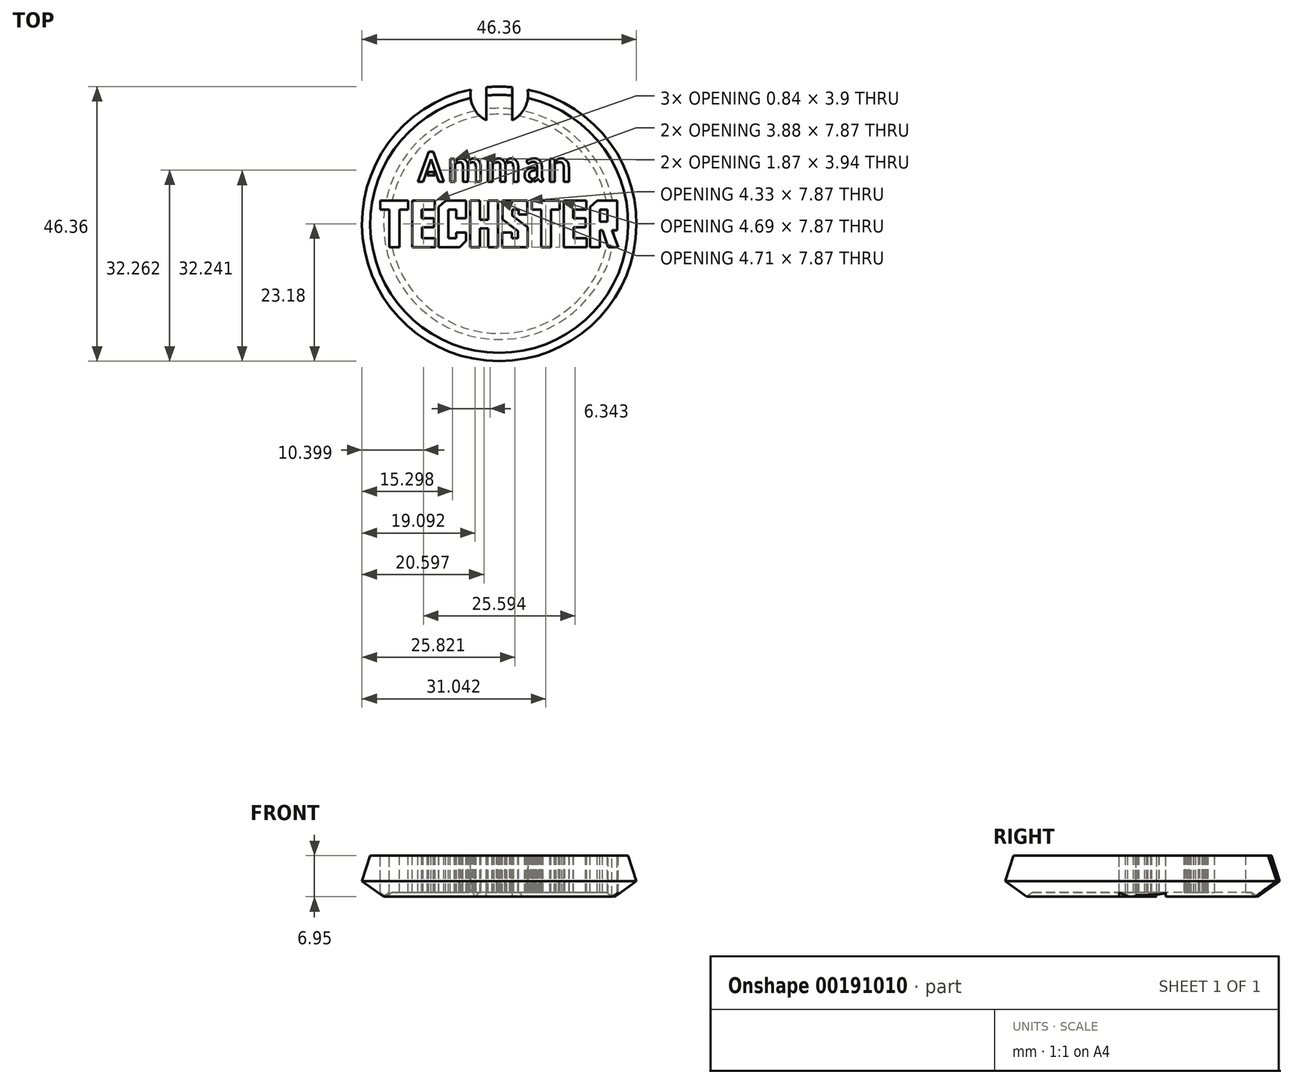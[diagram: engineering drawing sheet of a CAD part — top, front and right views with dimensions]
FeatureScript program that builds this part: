
annotation { "Feature Type Name" : "Feature", "Feature Type Description" : "" }
export const myFeature = defineFeature(function(context is Context, id is Id, definition is map)
    precondition{}
    {
        {
            var Q0;
            Q0=qCreatedBy(makeId("Front.planeOp"),FACE);
            var sketch = newSketch(context, id + "F0", { "sketchPlane" : qUnion([Q0])});
            skLineSegment(sketch, "E0.bottom", {"start": v(0, 0) * mm, "end": v(-19.52, 0) * mm});
            skLineSegment(sketch, "E0.top", {"start": v(0, 6.22) * mm, "end": v(-19.52, 6.22) * mm});
            skLineSegment(sketch, "E0.left", {"start": v(0, 0) * mm, "end": v(0, 6.22) * mm});
            skLineSegment(sketch, "E0.right", {"start": v(-19.52, 0) * mm, "end": v(-19.52, 6.22) * mm});
            skCircle(sketch, "E1.cCircle", {"center": v(-19.52, 3.1) * mm, "radius": 3.1 * mm, "construction": true});
            skLineSegment(sketch, "E1.0", {"start": v(-21.78, 6.22) * mm, "end": v(-17.27, 6.22) * mm});
            skLineSegment(sketch, "E1.1", {"start": v(-17.27, 6.22) * mm, "end": v(-15.87, 1.92) * mm});
            skLineSegment(sketch, "E1.2", {"start": v(-15.87, 1.92) * mm, "end": v(-19.52, -0.73) * mm});
            skLineSegment(sketch, "E1.3", {"start": v(-19.52, -0.73) * mm, "end": v(-23.18, 1.92) * mm});
            skLineSegment(sketch, "E1.4", {"start": v(-23.18, 1.92) * mm, "end": v(-21.78, 6.22) * mm});
            skPoint(sketch, "E1.0.midPoint", {"position": v(-19.52, 6.22) * mm});
            skSolve(sketch);
        }
        {
            var Q0;
            Q0 = qSketchRegion(id + "F0", true);
            var Q1;
            Q1=sQuery(id+"F0.wireOp",EDGE,"E0.left");
            revolve(context, id + "F1", {"entities" : qUnion([Q0]), "axis" : qUnion([Q1]), "revolveType" : RevolveType.FULL});
        }
        {
            var Q0;
            Q0=qCreatedBy(makeId("Top.planeOp"),FACE);
            cPlane(context, id + "F2", {"entities" : qUnion([Q0]), "cplaneType" : CPlaneType.OFFSET, "offset" : 8 * mm, "width" : 152.4 * mm, "height" : 152.4 * mm});
        }
        {
            var Q0;
            Q0=qCreatedBy(id+"F2.planeOp",FACE);
            var sketch = newSketch(context, id + "F3", { "sketchPlane" : qUnion([Q0])});
            skLineSegment(sketch, "E2", {"start": v(-15.39, 2.44) * mm, "end": v(-16.87, 2.44) * mm});
            skLineSegment(sketch, "E3", {"start": v(-16.87, 2.44) * mm, "end": v(-16.87, -3.94) * mm});
            skLineSegment(sketch, "E4", {"start": v(-16.87, -3.94) * mm, "end": v(-18.54, -3.94) * mm});
            skLineSegment(sketch, "E5", {"start": v(-18.54, -3.94) * mm, "end": v(-18.54, 2.44) * mm});
            skLineSegment(sketch, "E6", {"start": v(-18.54, 2.44) * mm, "end": v(-20.08, 2.44) * mm});
            skLineSegment(sketch, "E7", {"start": v(-20.08, 2.44) * mm, "end": v(-20.08, 3.94) * mm});
            skLineSegment(sketch, "E8", {"start": v(-20.08, 3.94) * mm, "end": v(-15.39, 3.94) * mm});
            skLineSegment(sketch, "E9", {"start": v(-15.39, 3.94) * mm, "end": v(-15.39, 2.44) * mm});
            skLineSegment(sketch, "E10", {"start": v(-14.72, 3.94) * mm, "end": v(-10.9, 3.94) * mm});
            skLineSegment(sketch, "E11", {"start": v(-10.9, 3.94) * mm, "end": v(-10.9, 2.44) * mm});
            skLineSegment(sketch, "E12", {"start": v(-10.9, 2.44) * mm, "end": v(-13.09, 2.44) * mm});
            skLineSegment(sketch, "E13", {"start": v(-13.09, 2.44) * mm, "end": v(-13.09, 0.92) * mm});
            skLineSegment(sketch, "E14", {"start": v(-13.09, 0.92) * mm, "end": v(-11, 0.92) * mm});
            skLineSegment(sketch, "E15", {"start": v(-11, 0.92) * mm, "end": v(-11, -0.55) * mm});
            skLineSegment(sketch, "E16", {"start": v(-11, -0.55) * mm, "end": v(-13.06, -0.55) * mm});
            skLineSegment(sketch, "E17", {"start": v(-13.06, -0.55) * mm, "end": v(-13.06, -2.44) * mm});
            skLineSegment(sketch, "E18", {"start": v(-13.06, -2.44) * mm, "end": v(-10.84, -2.44) * mm});
            skLineSegment(sketch, "E19", {"start": v(-10.84, -2.44) * mm, "end": v(-10.84, -3.94) * mm});
            skLineSegment(sketch, "E20", {"start": v(-10.84, -3.94) * mm, "end": v(-14.72, -3.94) * mm});
            skLineSegment(sketch, "E21", {"start": v(-14.72, -3.94) * mm, "end": v(-14.72, 3.94) * mm});
            skLineSegment(sketch, "E22", {"start": v(-7.25, -2.44) * mm, "end": v(-7.25, -1.49) * mm});
            skLineSegment(sketch, "E23", {"start": v(-7.25, -1.49) * mm, "end": v(-5.6, -1.49) * mm});
            skLineSegment(sketch, "E24", {"start": v(-5.6, -1.49) * mm, "end": v(-5.6, -2.85) * mm});
            skLineSegment(sketch, "E25", {"start": v(-5.6, -2.85) * mm, "end": v(-6.69, -3.94) * mm});
            skLineSegment(sketch, "E26", {"start": v(-6.69, -3.94) * mm, "end": v(-10.24, -3.94) * mm});
            skLineSegment(sketch, "E27", {"start": v(-10.24, -3.94) * mm, "end": v(-10.24, 2.85) * mm});
            skLineSegment(sketch, "E28", {"start": v(-10.24, 2.85) * mm, "end": v(-9.06, 3.94) * mm});
            skLineSegment(sketch, "E29", {"start": v(-9.06, 3.94) * mm, "end": v(-5.6, 3.94) * mm});
            skLineSegment(sketch, "E30", {"start": v(-5.6, 3.94) * mm, "end": v(-5.6, 0.96) * mm});
            skLineSegment(sketch, "E31", {"start": v(-5.6, 0.96) * mm, "end": v(-7.25, 0.96) * mm});
            skLineSegment(sketch, "E32", {"start": v(-7.25, 0.96) * mm, "end": v(-7.25, 2.44) * mm});
            skLineSegment(sketch, "E33", {"start": v(-7.25, 2.44) * mm, "end": v(-8.58, 2.44) * mm});
            skLineSegment(sketch, "E34", {"start": v(-8.58, 2.44) * mm, "end": v(-8.58, -2.44) * mm});
            skLineSegment(sketch, "E35", {"start": v(-8.58, -2.44) * mm, "end": v(-7.25, -2.44) * mm});
            skLineSegment(sketch, "E36", {"start": v(-3.3, 0.7) * mm, "end": v(-1.88, 0.7) * mm});
            skLineSegment(sketch, "E37", {"start": v(-1.88, 0.7) * mm, "end": v(-1.88, 3.94) * mm});
            skLineSegment(sketch, "E38", {"start": v(-1.88, 3.94) * mm, "end": v(-0.23, 3.94) * mm});
            skLineSegment(sketch, "E39", {"start": v(-0.23, 3.94) * mm, "end": v(-0.23, -3.94) * mm});
            skLineSegment(sketch, "E40", {"start": v(-0.23, -3.94) * mm, "end": v(-1.88, -3.94) * mm});
            skLineSegment(sketch, "E41", {"start": v(-1.88, -3.94) * mm, "end": v(-1.88, -0.79) * mm});
            skLineSegment(sketch, "E42", {"start": v(-1.88, -0.79) * mm, "end": v(-3.3, -0.79) * mm});
            skLineSegment(sketch, "E43", {"start": v(-3.3, -0.79) * mm, "end": v(-3.3, -3.94) * mm});
            skLineSegment(sketch, "E44", {"start": v(-3.3, -3.94) * mm, "end": v(-4.94, -3.94) * mm});
            skLineSegment(sketch, "E45", {"start": v(-4.94, -3.94) * mm, "end": v(-4.94, 3.94) * mm});
            skLineSegment(sketch, "E46", {"start": v(-4.94, 3.94) * mm, "end": v(-3.3, 3.94) * mm});
            skLineSegment(sketch, "E47", {"start": v(-3.3, 3.94) * mm, "end": v(-3.3, 0.7) * mm});
            skLineSegment(sketch, "E48", {"start": v(4.8, -3.94) * mm, "end": v(0.48, -3.94) * mm});
            skLineSegment(sketch, "E49", {"start": v(0.48, -3.94) * mm, "end": v(0.48, -1.49) * mm});
            skLineSegment(sketch, "E50", {"start": v(0.48, -1.49) * mm, "end": v(2.13, -1.49) * mm});
            skLineSegment(sketch, "E51", {"start": v(2.13, -1.49) * mm, "end": v(2.13, -2.44) * mm});
            skLineSegment(sketch, "E52", {"start": v(2.13, -2.44) * mm, "end": v(3.15, -2.44) * mm});
            skLineSegment(sketch, "E53", {"start": v(3.15, -2.44) * mm, "end": v(3.15, -1.2) * mm});
            skLineSegment(sketch, "E54", {"start": v(3.15, -1.2) * mm, "end": v(0.53, 0.78) * mm});
            skLineSegment(sketch, "E55", {"start": v(0.53, 0.78) * mm, "end": v(0.53, 3.94) * mm});
            skLineSegment(sketch, "E56", {"start": v(0.53, 3.94) * mm, "end": v(4.76, 3.94) * mm});
            skLineSegment(sketch, "E57", {"start": v(4.76, 3.94) * mm, "end": v(4.76, 1.6) * mm});
            skLineSegment(sketch, "E58", {"start": v(4.76, 1.6) * mm, "end": v(3.26, 1.6) * mm});
            skLineSegment(sketch, "E59", {"start": v(3.26, 1.6) * mm, "end": v(3.26, 2.43) * mm});
            skLineSegment(sketch, "E60", {"start": v(3.26, 2.43) * mm, "end": v(2.18, 2.43) * mm});
            skLineSegment(sketch, "E61", {"start": v(2.18, 2.43) * mm, "end": v(2.18, 1.4) * mm});
            skLineSegment(sketch, "E62", {"start": v(2.18, 1.4) * mm, "end": v(4.8, -0.57) * mm});
            skLineSegment(sketch, "E63", {"start": v(4.8, -0.57) * mm, "end": v(4.8, -3.94) * mm});
            skLineSegment(sketch, "E64", {"start": v(10.2, 2.44) * mm, "end": v(8.72, 2.44) * mm});
            skLineSegment(sketch, "E65", {"start": v(8.72, 2.44) * mm, "end": v(8.72, -3.94) * mm});
            skLineSegment(sketch, "E66", {"start": v(8.72, -3.94) * mm, "end": v(7.06, -3.94) * mm});
            skLineSegment(sketch, "E67", {"start": v(7.06, -3.94) * mm, "end": v(7.06, 2.44) * mm});
            skLineSegment(sketch, "E68", {"start": v(7.06, 2.44) * mm, "end": v(5.52, 2.44) * mm});
            skLineSegment(sketch, "E69", {"start": v(5.52, 2.44) * mm, "end": v(5.52, 3.94) * mm});
            skLineSegment(sketch, "E70", {"start": v(5.52, 3.94) * mm, "end": v(10.2, 3.94) * mm});
            skLineSegment(sketch, "E71", {"start": v(10.2, 3.94) * mm, "end": v(10.2, 2.44) * mm});
            skLineSegment(sketch, "E72", {"start": v(10.88, 3.94) * mm, "end": v(14.7, 3.94) * mm});
            skLineSegment(sketch, "E73", {"start": v(14.7, 3.94) * mm, "end": v(14.7, 2.44) * mm});
            skLineSegment(sketch, "E74", {"start": v(14.7, 2.44) * mm, "end": v(12.5, 2.44) * mm});
            skLineSegment(sketch, "E75", {"start": v(12.5, 2.44) * mm, "end": v(12.5, 0.92) * mm});
            skLineSegment(sketch, "E76", {"start": v(12.5, 0.92) * mm, "end": v(14.59, 0.92) * mm});
            skLineSegment(sketch, "E77", {"start": v(14.59, 0.92) * mm, "end": v(14.59, -0.55) * mm});
            skLineSegment(sketch, "E78", {"start": v(14.59, -0.55) * mm, "end": v(12.53, -0.55) * mm});
            skLineSegment(sketch, "E79", {"start": v(12.53, -0.55) * mm, "end": v(12.53, -2.44) * mm});
            skLineSegment(sketch, "E80", {"start": v(12.53, -2.44) * mm, "end": v(14.75, -2.44) * mm});
            skLineSegment(sketch, "E81", {"start": v(14.75, -2.44) * mm, "end": v(14.75, -3.94) * mm});
            skLineSegment(sketch, "E82", {"start": v(14.75, -3.94) * mm, "end": v(10.88, -3.94) * mm});
            skLineSegment(sketch, "E83", {"start": v(10.88, -3.94) * mm, "end": v(10.88, 3.94) * mm});
            skLineSegment(sketch, "E84", {"start": v(18.42, -3.94) * mm, "end": v(17.44, -1.09) * mm});
            skLineSegment(sketch, "E85", {"start": v(17.44, -1.09) * mm, "end": v(17, -1.09) * mm});
            skLineSegment(sketch, "E86", {"start": v(17, -1.09) * mm, "end": v(17, -3.94) * mm});
            skLineSegment(sketch, "E87", {"start": v(17, -3.94) * mm, "end": v(15.36, -3.94) * mm});
            skLineSegment(sketch, "E88", {"start": v(15.36, -3.94) * mm, "end": v(15.36, 2.83) * mm});
            skLineSegment(sketch, "E89", {"start": v(15.36, 2.83) * mm, "end": v(16.55, 3.94) * mm});
            skLineSegment(sketch, "E90", {"start": v(16.55, 3.94) * mm, "end": v(19.92, 3.94) * mm});
            skLineSegment(sketch, "E91", {"start": v(19.92, 3.94) * mm, "end": v(19.92, -1.07) * mm});
            skLineSegment(sketch, "E92", {"start": v(19.92, -1.07) * mm, "end": v(19.03, -1.07) * mm});
            skLineSegment(sketch, "E93", {"start": v(19.03, -1.07) * mm, "end": v(20.08, -3.94) * mm});
            skLineSegment(sketch, "E94", {"start": v(20.08, -3.94) * mm, "end": v(18.42, -3.94) * mm});
            skLineSegment(sketch, "E95", {"start": v(18.27, 0.39) * mm, "end": v(18.27, 2.44) * mm});
            skLineSegment(sketch, "E96", {"start": v(18.27, 2.44) * mm, "end": v(17, 2.44) * mm});
            skLineSegment(sketch, "E97", {"start": v(17, 2.44) * mm, "end": v(17, 0.39) * mm});
            skLineSegment(sketch, "E98", {"start": v(17, 0.39) * mm, "end": v(18.27, 0.39) * mm});
            skSolve(sketch);
        }
        {
            var Q0;
            Q0 = qSketchRegion(id + "F3", true);
            extrude(context, id + "F4", {"entities" : qUnion([Q0]), "operationType" : NewBodyOperationType.REMOVE, "oppositeDirection" : true, "depth" : 25.4 * mm});
        }
        {
            var Q0;
            Q0=qCreatedBy(id+"F2.planeOp",FACE);
            var sketch = newSketch(context, id + "F5", { "sketchPlane" : qUnion([Q0])});
            skLineSegment(sketch, "E99.top", {"start": v(2.2, 26.67) * mm, "end": v(-2.2, 26.67) * mm});
            skLineSegment(sketch, "E99.left", {"start": v(2.2, 16.95) * mm, "end": v(2.2, 26.67) * mm});
            skLineSegment(sketch, "E99.right", {"start": v(-2.2, 16.95) * mm, "end": v(-2.2, 26.67) * mm});
            skPoint(sketch, "E99.middle", {"position": v(0, 21.81) * mm});
            skArc(sketch, "E100", {"start": v(2.2, 17.48) * mm, "mid": v(0, 26.67) * mm, "end": v(-2.2, 17.48) * mm});
            skSolve(sketch);
        }
        {
            var Q0;
            Q0 = qSketchRegion(id + "F5", true);
            extrude(context, id + "F6", {"entities" : qUnion([Q0]), "operationType" : NewBodyOperationType.REMOVE, "oppositeDirection" : true, "depth" : 25.4 * mm});
        }
        {
            var Q0;
            Q0=qCreatedBy(id+"F2.planeOp",FACE);
            var sketch = newSketch(context, id + "F7", { "sketchPlane" : qUnion([Q0])});
            skText(sketch, "E101", { "text": "Amman", "fontName": "AllertaStencil-Regular.ttf"});
            const initialGuessF7  = {"E101": [-0.01415, 0.00711, 1, 0, 0.0051]};
            skSetInitialGuess(sketch, initialGuessF7);
            skSolve(sketch);
        }
        {
            var Q0;
            Q0 = qSketchRegion(id + "F7", true);
            extrude(context, id + "F8", {"entities" : qUnion([Q0]), "operationType" : NewBodyOperationType.REMOVE, "oppositeDirection" : true, "depth" : 25.4 * mm});
        }
    });
